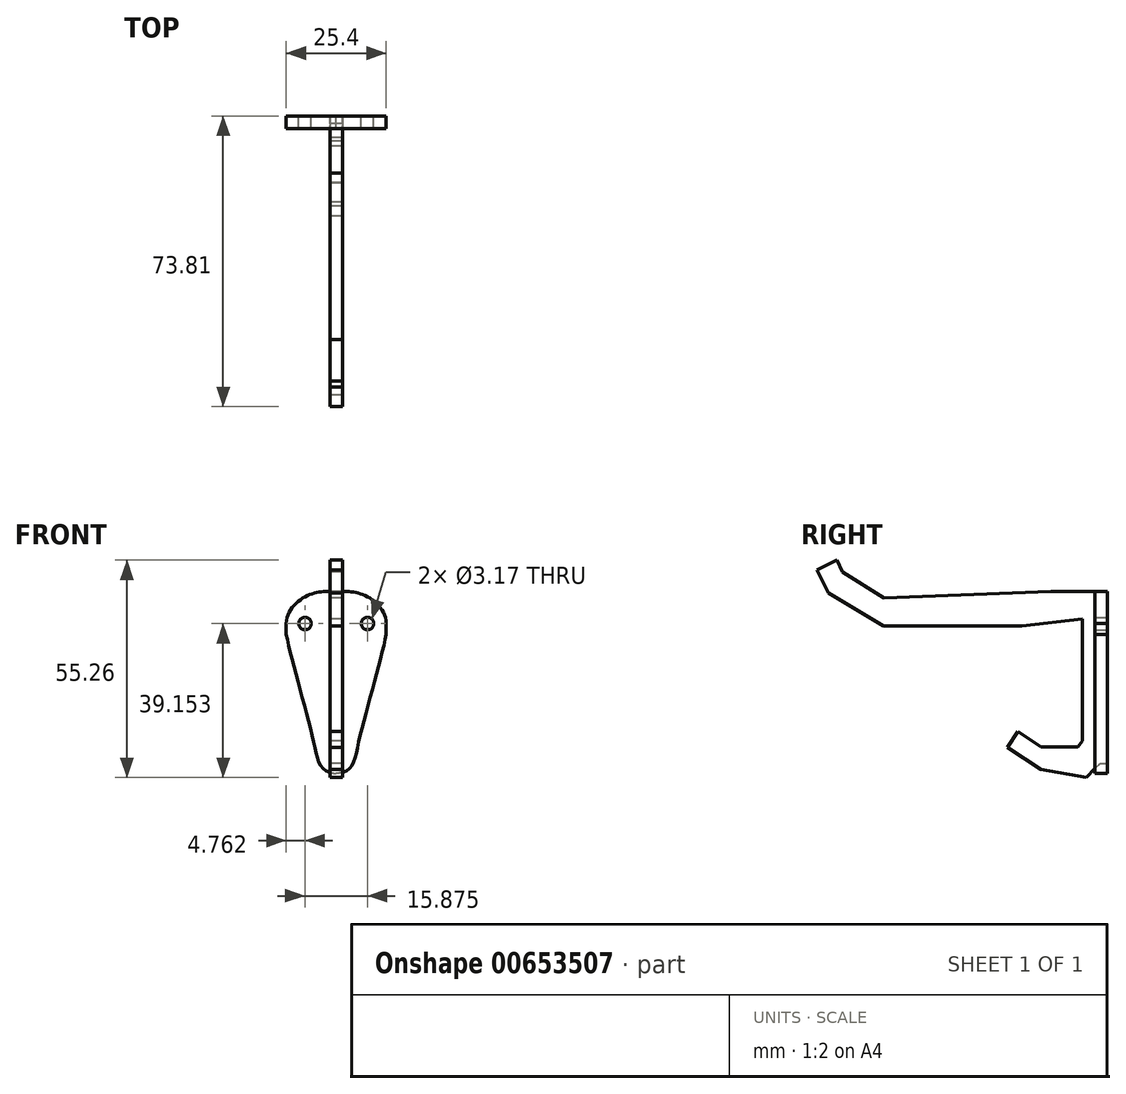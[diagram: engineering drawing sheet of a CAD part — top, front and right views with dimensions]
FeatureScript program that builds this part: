
annotation { "Feature Type Name" : "Feature", "Feature Type Description" : "" }
export const myFeature = defineFeature(function(context is Context, id is Id, definition is map)
    precondition{}
    {
        {
            var Q0;
            Q0=qCreatedBy(makeId("Front.planeOp"),FACE);
            var sketch = newSketch(context, id + "F0", { "sketchPlane" : qUnion([Q0])});
            skLineSegment(sketch, "E0", {"start": v(-12.7, 9.26) * mm, "end": v(-12.7, 6.5) * mm});
            skFitSpline(sketch, "E1", {"points": [v(-12.7, 9.26) * mm, v(-6.7, 16.58) * mm, v(0, 17.38) * mm], "startDerivative": vector(0.72, 20.06) * mm, "endDerivative": vector(13.95, 0.05) * mm});
            skFitSpline(sketch, "E2", {"points": [v(-12.7, 6.5) * mm, v(-5.56, -21.55) * mm, v(0, -28.89) * mm], "startDerivative": vector(5.68, -30.5) * mm, "endDerivative": vector(36.85, -2.9) * mm});
            skFitSpline(sketch, "E3.MirrorCS", {"points": [v(12.7, 9.26) * mm, v(6.7, 16.58) * mm, v(0, 17.38) * mm], "startDerivative": vector(-0.72, 20.06) * mm, "endDerivative": vector(-13.95, 0.05) * mm});
            skLineSegment(sketch, "E4.MirrorCS", {"start": v(12.7, 9.26) * mm, "end": v(12.7, 6.5) * mm});
            skFitSpline(sketch, "E5.MirrorCS", {"points": [v(12.7, 6.5) * mm, v(5.56, -21.55) * mm, v(0, -28.89) * mm], "startDerivative": vector(-5.68, -30.5) * mm, "endDerivative": vector(-36.85, -2.9) * mm});
            skCircle(sketch, "E6", {"center": v(-7.94, 9.21) * mm, "radius": 1.59 * mm});
            skCircle(sketch, "E7", {"center": v(7.94, 9.21) * mm, "radius": 1.59 * mm});
            skSolve(sketch);
        }
        {
            var Q0;
            Q0=qSketchRegion(id+"F0",true);
            extrude(context, id + "F1", {"entities" : qUnion([Q0]), "depth" : 3.17 * mm, "offsetDistance" : 25.4 * mm});
        }
        {
            var Q0;
            Q0=qCreatedBy(makeId("Right.planeOp"),FACE);
            var sketch = newSketch(context, id + "F2", { "sketchPlane" : qUnion([Q0])});
            skLineSegment(sketch, "E8", {"start": v(0, 17.38) * mm, "end": v(-14.4, 17.38) * mm});
            skLineSegment(sketch, "E9", {"start": v(-14.4, 17.38) * mm, "end": v(-56.76, 15.72) * mm});
            skLineSegment(sketch, "E10", {"start": v(-56.76, 15.72) * mm, "end": v(-67.33, 22.32) * mm});
            skLineSegment(sketch, "E11", {"start": v(-67.33, 22.32) * mm, "end": v(-68.8, 25.32) * mm});
            skLineSegment(sketch, "E12", {"start": v(-68.8, 25.32) * mm, "end": v(-73.8, 22.87) * mm});
            skLineSegment(sketch, "E13", {"start": v(-73.8, 22.87) * mm, "end": v(-70.9, 16.93) * mm});
            skLineSegment(sketch, "E14", {"start": v(-70.9, 16.93) * mm, "end": v(-56.95, 8.62) * mm});
            skLineSegment(sketch, "E15", {"start": v(-56.95, 8.62) * mm, "end": v(-21.8, 8.62) * mm});
            skLineSegment(sketch, "E16", {"start": v(-6.35, 10.39) * mm, "end": v(-21.8, 8.62) * mm});
            skLineSegment(sketch, "E17", {"start": v(-6.35, 10.39) * mm, "end": v(-6.35, -20.64) * mm});
            skLineSegment(sketch, "E18", {"start": v(-6.35, -20.64) * mm, "end": v(-7.57, -22.14) * mm});
            skLineSegment(sketch, "E19", {"start": v(-7.57, -22.14) * mm, "end": v(-16.92, -22.14) * mm});
            skLineSegment(sketch, "E20", {"start": v(-16.92, -22.14) * mm, "end": v(-22.82, -18.25) * mm});
            skLineSegment(sketch, "E21", {"start": v(-22.82, -18.25) * mm, "end": v(-25.44, -22.2) * mm});
            skLineSegment(sketch, "E22", {"start": v(-25.44, -22.2) * mm, "end": v(-16.94, -27.81) * mm});
            skLineSegment(sketch, "E23", {"start": v(-16.94, -27.81) * mm, "end": v(-5.4, -29.94) * mm});
            skLineSegment(sketch, "E24", {"start": v(-5.4, -29.94) * mm, "end": v(-1.86, -26.28) * mm});
            skLineSegment(sketch, "E25", {"start": v(-1.86, -26.28) * mm, "end": v(0, -26.28) * mm});
            skLineSegment(sketch, "E26", {"start": v(0, -26.28) * mm, "end": v(0, 17.38) * mm});
            skSolve(sketch);
        }
        {
            var Q0;
            Q0=makeQuery(id+"F2.imprint","IMPRINT",FACE,{"disambiguationData":[TD([[makeQuery(id+"F2.imprint","IMPRINT",EDGE,{"derivedFrom":sQuery(id+"F2.wireOp",EDGE,"E8")}),1.0]])]});
            extrude(context, id + "F3", {"entities" : qUnion([Q0]), "depth" : 1.59 * mm, "hasSecondDirection" : true, "secondDirectionOppositeDirection" : true, "secondDirectionDepth" : 1.59 * mm});
        }
    });
